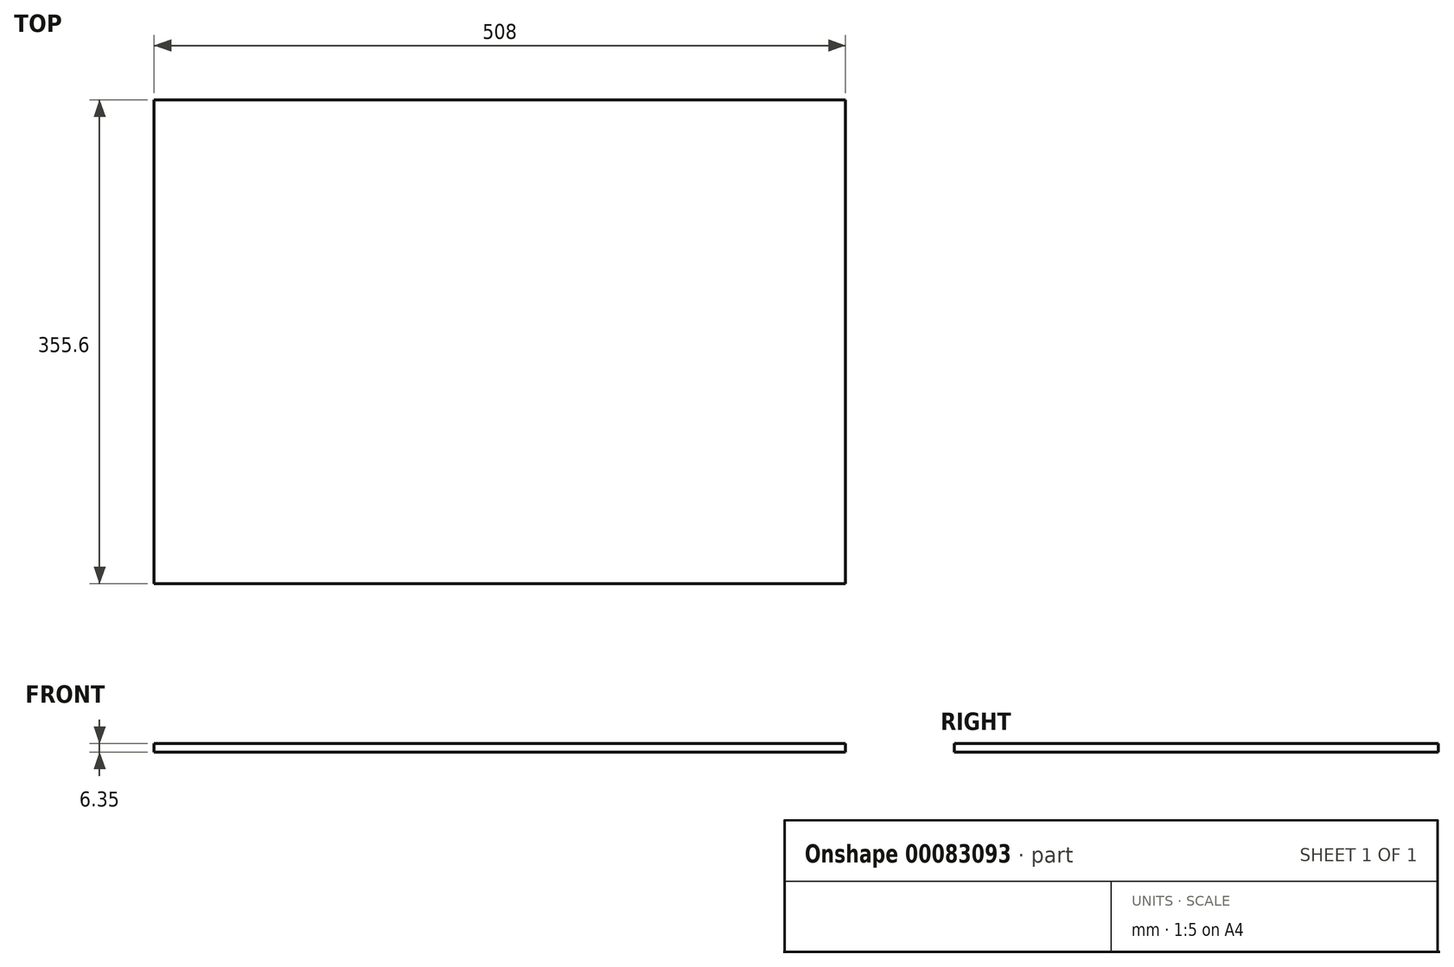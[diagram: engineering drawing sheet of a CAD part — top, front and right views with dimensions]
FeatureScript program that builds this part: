
annotation { "Feature Type Name" : "Feature", "Feature Type Description" : "" }
export const myFeature = defineFeature(function(context is Context, id is Id, definition is map)
    precondition{}
    {
        {
            var Q0;
            Q0=qCreatedBy(makeId("Top.planeOp"),FACE);
            var sketch = newSketch(context, id + "F0", { "sketchPlane" : qUnion([Q0])});
            skLineSegment(sketch, "E0.bottom", {"start": v(-248.62, 219.82) * mm, "end": v(259.38, 219.82) * mm});
            skLineSegment(sketch, "E0.top", {"start": v(-248.62, -135.78) * mm, "end": v(259.38, -135.78) * mm});
            skLineSegment(sketch, "E0.left", {"start": v(-248.62, 219.82) * mm, "end": v(-248.62, -135.78) * mm});
            skLineSegment(sketch, "E0.right", {"start": v(259.38, 219.82) * mm, "end": v(259.38, -135.78) * mm});
            skSolve(sketch);
        }
        {
            var Q0;
            Q0=makeQuery(id+"F0.imprint","IMPRINT",FACE,{"disambiguationData":[TD([[makeQuery(id+"F0.imprint","IMPRINT",EDGE,{"derivedFrom":sQuery(id+"F0.wireOp",EDGE,"E0.bottom")}),-1.0]])]});
            extrude(context, id + "F1", {"entities" : qUnion([Q0]), "depth" : 6.35 * mm});
        }
    });
